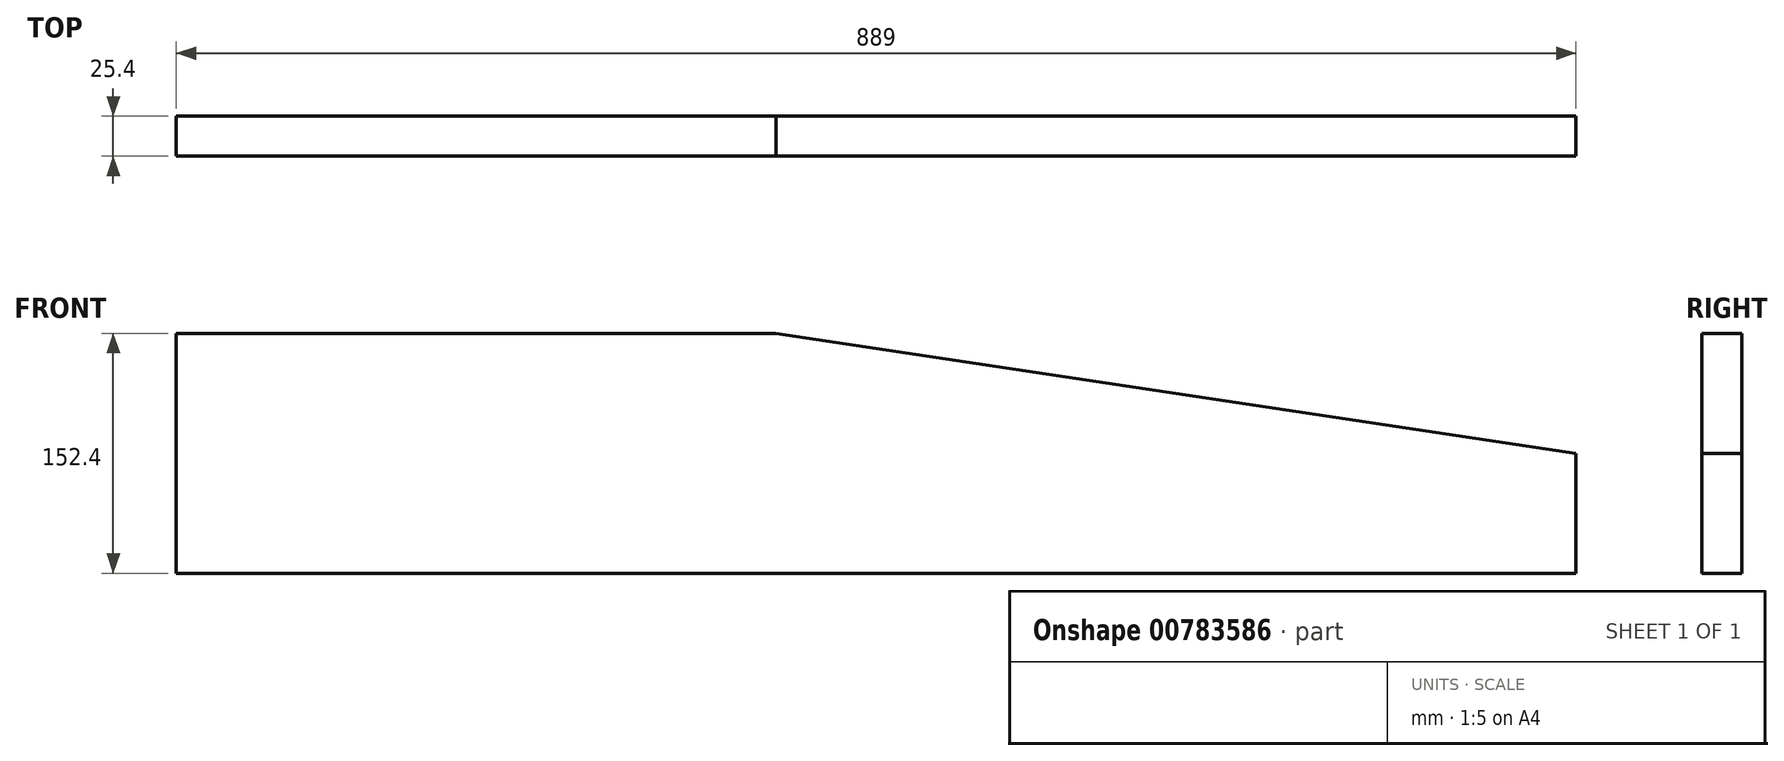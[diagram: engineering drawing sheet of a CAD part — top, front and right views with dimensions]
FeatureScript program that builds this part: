
annotation { "Feature Type Name" : "Feature", "Feature Type Description" : "" }
export const myFeature = defineFeature(function(context is Context, id is Id, definition is map)
    precondition{}
    {
        {
            var Q0;
            Q0=qCreatedBy(makeId("Front.planeOp"),FACE);
            var sketch = newSketch(context, id + "F0", { "sketchPlane" : qUnion([Q0])});
            skLineSegment(sketch, "E0.bottom", {"start": v(0, 0) * mm, "end": v(889, 0) * mm});
            skLineSegment(sketch, "E0.top", {"start": v(0, 152.4) * mm, "end": v(381, 152.4) * mm});
            skLineSegment(sketch, "E0.left", {"start": v(0, 0) * mm, "end": v(0, 152.4) * mm});
            skLineSegment(sketch, "E0.right", {"start": v(889, 0) * mm, "end": v(889, 76.2) * mm});
            skLineSegment(sketch, "E1", {"start": v(889, 76.2) * mm, "end": v(381, 152.4) * mm});
            skSolve(sketch);
        }
        {
            var Q0;
            Q0=makeQuery(id+"F0.imprint","IMPRINT",FACE,{"disambiguationData":[TD([[makeQuery(id+"F0.imprint","IMPRINT",EDGE,{"derivedFrom":sQuery(id+"F0.wireOp",EDGE,"E0.bottom")}),1.0]])]});
            extrude(context, id + "F1", {"entities" : qUnion([Q0]), "depth" : 25.4 * mm, "offsetDistance" : 25.4 * mm});
        }
    });
